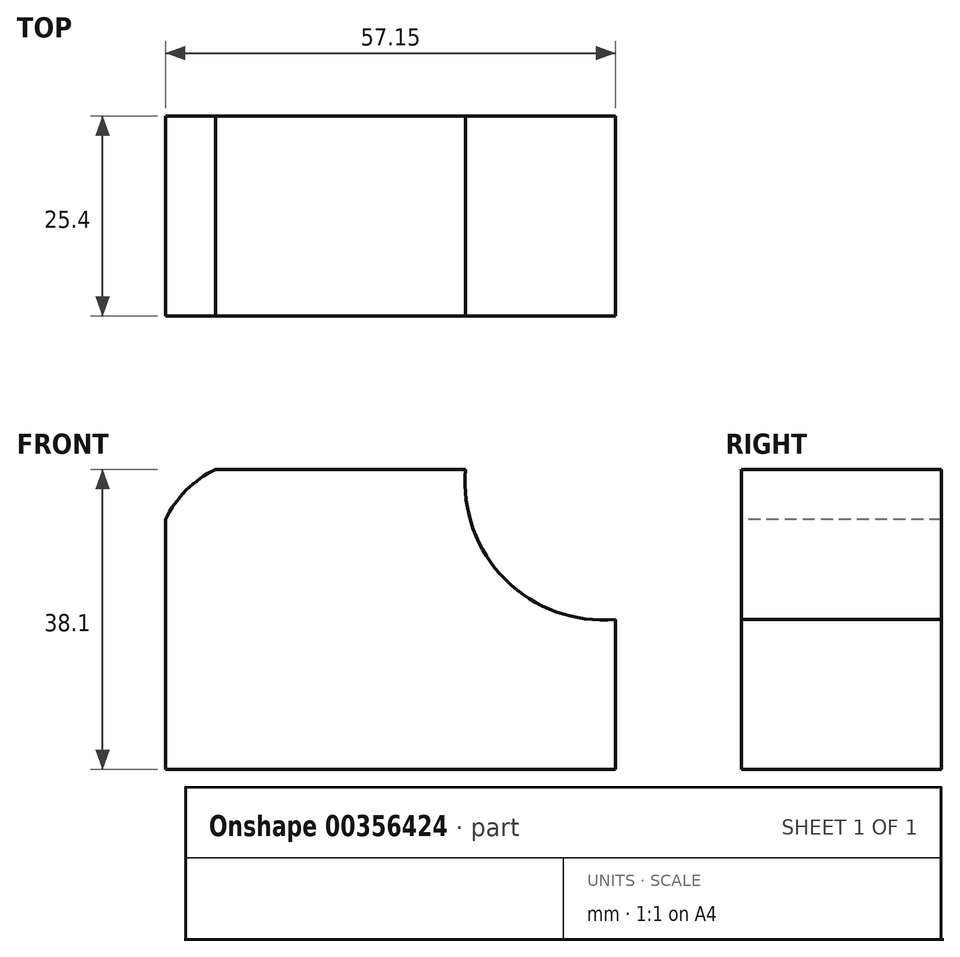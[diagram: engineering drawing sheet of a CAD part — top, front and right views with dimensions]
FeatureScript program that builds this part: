
annotation { "Feature Type Name" : "Feature", "Feature Type Description" : "" }
export const myFeature = defineFeature(function(context is Context, id is Id, definition is map)
    precondition{}
    {
        {
            var Q0;
            Q0=qCreatedBy(makeId("Front.planeOp"),FACE);
            var sketch = newSketch(context, id + "F0", { "sketchPlane" : qUnion([Q0])});
            skLineSegment(sketch, "E0", {"start": v(0, 38.1) * mm, "end": v(0, 0) * mm});
            skLineSegment(sketch, "E1", {"start": v(0, 0) * mm, "end": v(57.15, 0) * mm});
            skLineSegment(sketch, "E2", {"start": v(57.15, 0) * mm, "end": v(57.15, 38.1) * mm});
            skLineSegment(sketch, "E3", {"start": v(57.15, 38.1) * mm, "end": v(0, 38.1) * mm});
            skSolve(sketch);
        }
        {
            var Q0;
            Q0 = qSketchRegion(id + "F0", true);
            extrude(context, id + "F1", {"entities" : qUnion([Q0]), "depth" : 25.4 * mm});
        }
        {
            var Q0;
            Q0=makeQuery(id+"F1.opExtrude","CAP_FACE",FACE,{"disambiguationData":[OSD([sQuery(id+"F0.wireOp",EDGE,"E0"),sQuery(id+"F0.wireOp",EDGE,"E1"),sQuery(id+"F0.wireOp",EDGE,"E2"),sQuery(id+"F0.wireOp",EDGE,"E3")])],"isStart":false});
            var sketch = newSketch(context, id + "F2", { "sketchPlane" : qUnion([Q0])});
            skArc(sketch, "E4", {"start": v(38.1, 38.1) * mm, "mid": v(43.17, 24.12) * mm, "end": v(57.15, 19.05) * mm});
            skSolve(sketch);
        }
        {
            var Q0;
            Q0 = qSketchRegion(id + "F2", true);
            var Q1;
            {var subQ0=sQuery(id+"F2.wireOp",EDGE,"E4");Q1=makeQuery(id+"F2.imprint","IMPRINT",FACE,{"disambiguationData":[TD([[makeQuery(id+"F2.imprint","IMPRINT",EDGE,{"derivedFrom":subQ0}),1.0]])]});}
            extrude(context, id + "F3", {"entities" : qUnion([Q0, Q1]), "operationType" : NewBodyOperationType.REMOVE, "oppositeDirection" : true, "depth" : 25.4 * mm});
        }
        {
            var Q0;
            Q0=makeQuery(id+"F1.opExtrude","CAP_FACE",FACE,{"disambiguationData":[OSD([sQuery(id+"F0.wireOp",EDGE,"E0"),sQuery(id+"F0.wireOp",EDGE,"E1"),sQuery(id+"F0.wireOp",EDGE,"E2"),sQuery(id+"F0.wireOp",EDGE,"E3")])],"isStart":false});
            var sketch = newSketch(context, id + "F4", { "sketchPlane" : qUnion([Q0])});
            skArc(sketch, "E5", {"start": v(6.35, 38.1) * mm, "mid": v(2.62, 35.48) * mm, "end": v(0, 31.75) * mm});
            skSolve(sketch);
        }
        {
            var Q0;
            Q0 = qSketchRegion(id + "F4", true);
            var Q1;
            {var subQ0=sQuery(id+"F4.wireOp",EDGE,"E5");Q1=makeQuery(id+"F4.imprint","IMPRINT",FACE,{"disambiguationData":[TD([[makeQuery(id+"F4.imprint","IMPRINT",EDGE,{"derivedFrom":subQ0}),-1.0]])]});}
            extrude(context, id + "F5", {"entities" : qUnion([Q0, Q1]), "operationType" : NewBodyOperationType.REMOVE, "oppositeDirection" : true, "depth" : 25.4 * mm});
        }
    });
